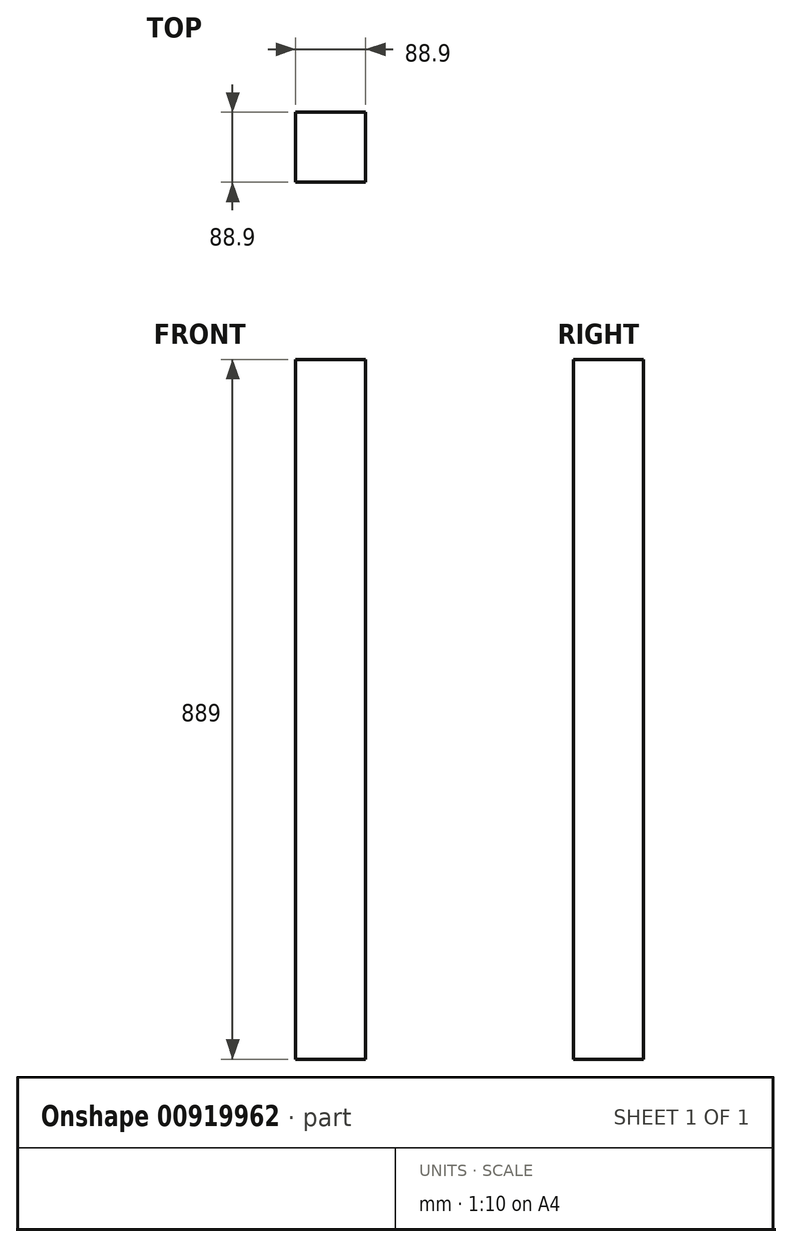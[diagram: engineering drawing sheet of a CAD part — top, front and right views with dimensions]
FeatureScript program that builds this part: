
annotation { "Feature Type Name" : "Feature", "Feature Type Description" : "" }
export const myFeature = defineFeature(function(context is Context, id is Id, definition is map)
    precondition{}
    {
        {
            var Q0;
            Q0=qCreatedBy(makeId("Top.planeOp"),FACE);
            var sketch = newSketch(context, id + "F0", { "sketchPlane" : qUnion([Q0])});
            skLineSegment(sketch, "E0.bottom", {"start": v(-44.45, 44.45) * mm, "end": v(44.45, 44.45) * mm});
            skLineSegment(sketch, "E0.top", {"start": v(-44.45, -44.45) * mm, "end": v(44.45, -44.45) * mm});
            skLineSegment(sketch, "E0.left", {"start": v(-44.45, 44.45) * mm, "end": v(-44.45, -44.45) * mm});
            skLineSegment(sketch, "E0.right", {"start": v(44.45, 44.45) * mm, "end": v(44.45, -44.45) * mm});
            skPoint(sketch, "E1", {"position": v(0, 44.45) * mm});
            skPoint(sketch, "E2", {"position": v(44.45, 0) * mm});
            skSolve(sketch);
        }
        {
            var Q0;
            Q0 = qSketchRegion(id + "F0", true);
            extrude(context, id + "F1", {"entities" : qUnion([Q0]), "depth" : 889 * mm, "offsetDistance" : 25 * mm});
        }
        {
            var Q0;
            Q0=makeQuery(id+"F1.opExtrude","SWEPT_BODY",BODY,{"disambiguationData":[OSD([sQuery(id+"F0.wireOp",EDGE,"E0.bottom"),sQuery(id+"F0.wireOp",EDGE,"E0.top"),sQuery(id+"F0.wireOp",EDGE,"E0.left"),sQuery(id+"F0.wireOp",EDGE,"E0.right")])]});
            transform(context, id + "F2", {"entities" : qUnion([Q0]), "transformType" : TransformType.TRANSLATION_3D, "dx" : 0 * mm, "dy" : 0 * mm, "dz" : 0 * mm, "makeCopy" : true});
        }
        {
            var Q0;
            Q0=makeQuery(id+"F2.opPattern","COPY",BODY,{"derivedFrom":makeQuery(id+"F1.opExtrude","SWEPT_BODY",BODY,{"disambiguationData":[OSD([sQuery(id+"F0.wireOp",EDGE,"E0.bottom"),sQuery(id+"F0.wireOp",EDGE,"E0.top"),sQuery(id+"F0.wireOp",EDGE,"E0.left"),sQuery(id+"F0.wireOp",EDGE,"E0.right")])]}),"instanceName":"1"});
            deleteBodies(context, id + "F3", {"entities" : qUnion([Q0])});
        }
    });
